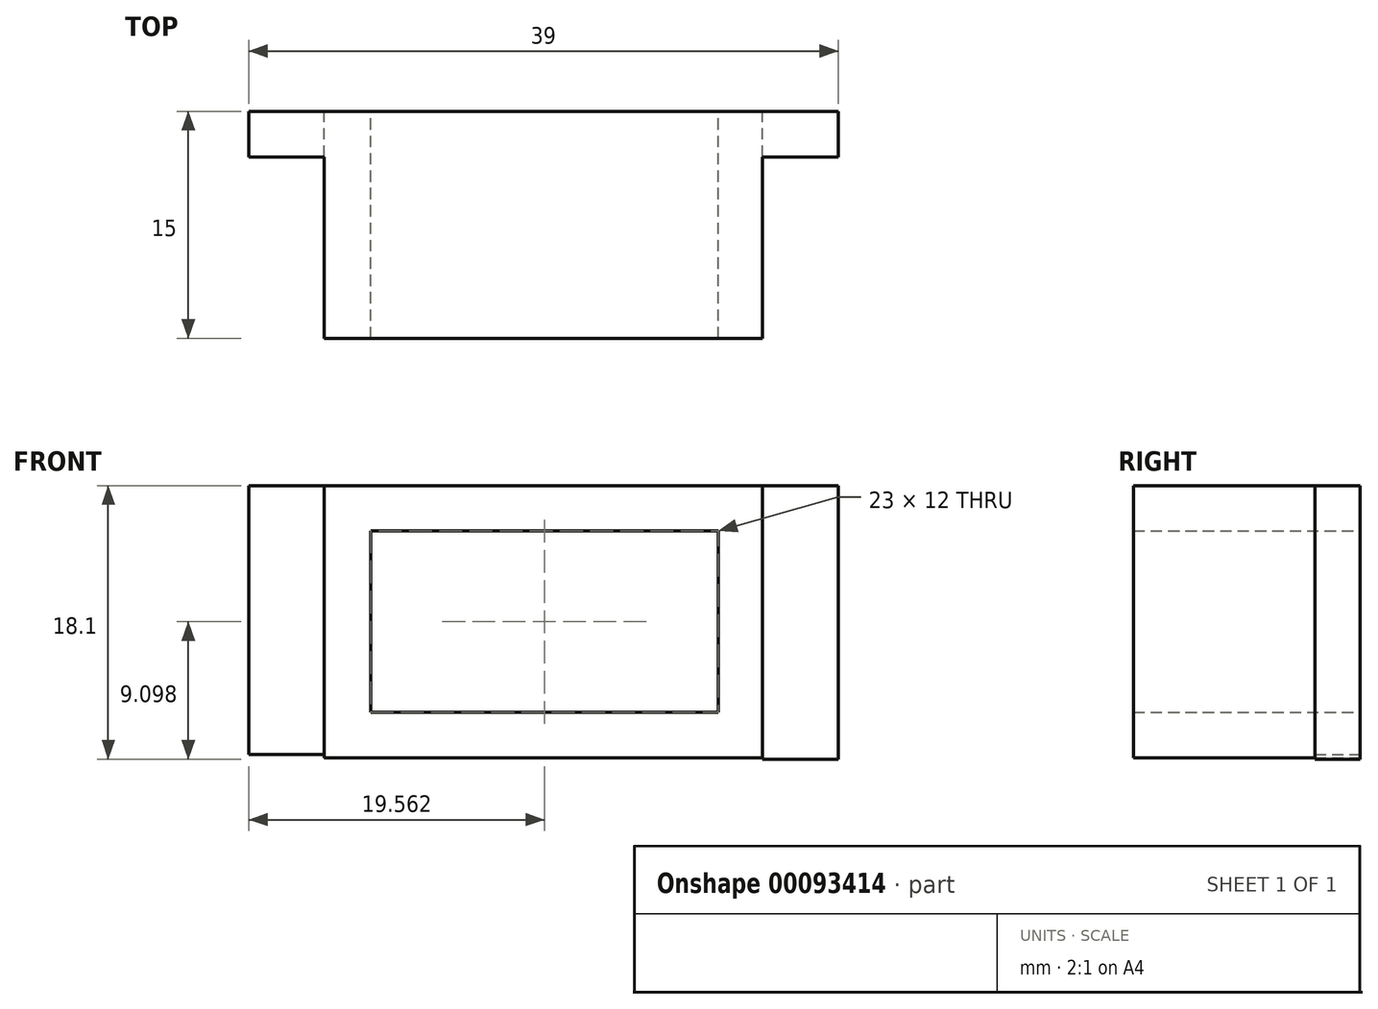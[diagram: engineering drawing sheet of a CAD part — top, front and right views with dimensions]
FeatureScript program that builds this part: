
annotation { "Feature Type Name" : "Feature", "Feature Type Description" : "" }
export const myFeature = defineFeature(function(context is Context, id is Id, definition is map)
    precondition{}
    {
        {
            var Q0;
            Q0=qCreatedBy(makeId("Front.planeOp"),FACE);
            var sketch = newSketch(context, id + "F0", { "sketchPlane" : qUnion([Q0])});
            skLineSegment(sketch, "E0.bottom", {"start": v(9.87, 31.68) * mm, "end": v(-13.13, 31.68) * mm});
            skLineSegment(sketch, "E0.top", {"start": v(9.87, 43.68) * mm, "end": v(-13.13, 43.68) * mm});
            skLineSegment(sketch, "E0.left", {"start": v(9.87, 31.68) * mm, "end": v(9.87, 43.68) * mm});
            skLineSegment(sketch, "E0.right", {"start": v(-13.13, 31.68) * mm, "end": v(-13.13, 43.68) * mm});
            skPoint(sketch, "E0.middle", {"position": v(-1.63, 37.68) * mm});
            skLineSegment(sketch, "E1.bottom", {"start": v(-16.2, 46.68) * mm, "end": v(12.8, 46.68) * mm});
            skLineSegment(sketch, "E1.top", {"start": v(-16.2, 28.68) * mm, "end": v(12.8, 28.68) * mm});
            skLineSegment(sketch, "E1.left", {"start": v(-16.2, 46.68) * mm, "end": v(-16.2, 28.68) * mm});
            skLineSegment(sketch, "E1.right", {"start": v(12.8, 46.68) * mm, "end": v(12.8, 28.68) * mm});
            skLineSegment(sketch, "E2.bottom", {"start": v(12.8, 46.68) * mm, "end": v(17.8, 46.68) * mm});
            skLineSegment(sketch, "E2.top", {"start": v(12.8, 28.58) * mm, "end": v(17.8, 28.58) * mm});
            skLineSegment(sketch, "E2.left", {"start": v(12.8, 46.68) * mm, "end": v(12.8, 28.58) * mm});
            skLineSegment(sketch, "E2.right", {"start": v(17.8, 46.68) * mm, "end": v(17.8, 28.58) * mm});
            skLineSegment(sketch, "E3.bottom", {"start": v(-16.2, 46.68) * mm, "end": v(-21.2, 46.68) * mm});
            skLineSegment(sketch, "E3.top", {"start": v(-16.2, 28.9) * mm, "end": v(-21.2, 28.9) * mm});
            skLineSegment(sketch, "E3.left", {"start": v(-16.2, 46.68) * mm, "end": v(-16.2, 28.9) * mm});
            skLineSegment(sketch, "E3.right", {"start": v(-21.2, 46.68) * mm, "end": v(-21.2, 28.9) * mm});
            skSolve(sketch);
        }
        {
            var Q0;
            Q0=makeQuery(id+"F0.imprint","IMPRINT",FACE,{"disambiguationData":[TD([[makeQuery(id+"F0.imprint","IMPRINT",EDGE,{"derivedFrom":sQuery(id+"F0.wireOp",EDGE,"E0.bottom")}),1.0]])]});
            extrude(context, id + "F1", {"entities" : qUnion([Q0]), "depth" : 15 * mm});
        }
        {
            var Q0;
            Q0=makeQuery(id+"F0.imprint","IMPRINT",FACE,{"disambiguationData":[TD([[makeQuery(id+"F0.imprint","IMPRINT",EDGE,{"derivedFrom":sQuery(id+"F0.wireOp",EDGE,"E3.bottom")}),1.0]])]});
            var Q1;
            {var subQ3=sQuery(id+"F0.wireOp",EDGE,"E2.bottom");Q1=makeQuery(id+"F0.imprint","IMPRINT",FACE,{"disambiguationData":[TD([[makeQuery(id+"F0.imprint","IMPRINT",EDGE,{"derivedFrom":subQ3}),-1.0]])]});}
            extrude(context, id + "F2", {"entities" : qUnion([Q0, Q1]), "operationType" : NewBodyOperationType.ADD, "depth" : 3 * mm});
        }
    });
